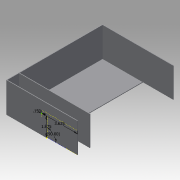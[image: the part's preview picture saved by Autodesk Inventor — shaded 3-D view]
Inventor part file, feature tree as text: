
AUTODESK INVENTOR PART (.ipt)
format: ipt  version: 2016 (Build 200138000, 138)  size: 138,752 bytes
history: native  units: in
note: dims shown in document units (in); Inventor stores cm internally (conversion verified against a paired STEP export)
features: sketch x6, extrude x4
ambient origin geometry x8: Origin, YZ Plane, XZ Plane, XY Plane, X Axis, Y Axis, Z Axis, Center Point
bodies: Solid1 (feature_tree)
feature tree (10):
  sketch  "Sketch1"  dims[d0=4.125in d1=9.8125in]
  extrude  "Extrusion1"  Depth=9.8125in
  extrude  "Extrusion2"  Depth=7.25in
  extrude  "Extrusion3"  Depth=7.25in
  extrude  "Extrusion4"  Depth=0.0625in
  sketch  "Sketch6"  dims[d12=3.0in d13=0.0in d14=1.25in d15=0.0625in d16=7.1875in d17=0.0in d18=2.0in d19=0.0in d20=1.875in d21=90.0deg d22=3.625in d23=0.15in]
  sketch  "Sketch2"  dims[d2=0.0625in d3=0.0in d6=7.25in]
  sketch  "Sketch3"  dims[d7=0.0625in d8=7.25in]
  sketch  "Sketch4"  dims[d9=0.0625in d10=0.0625in]
  sketch  "Sketch5"  dims[d11=12.0in]
